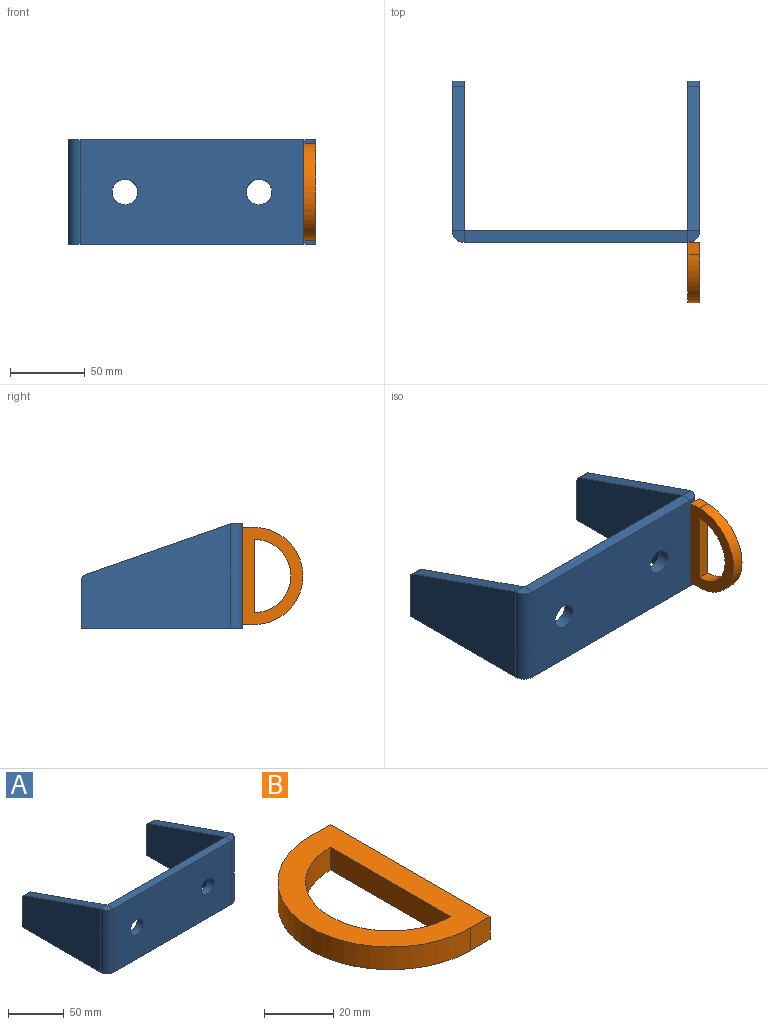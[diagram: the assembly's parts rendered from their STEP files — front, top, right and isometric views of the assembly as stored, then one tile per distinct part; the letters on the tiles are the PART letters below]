
ASSEMBLY  parts=2 mates=1
PART A: 26 faces, bbox 166x108x70 mm
  f0: plane 149.98x8mm, normal (0,0,-1), area 1199.8mm2, adj f4,f5,f13,f23
  f1: plane 149.99x8mm, normal (0,0,1), area 1199.8mm2, adj f4,f5,f12,f22
  f2: cylinder r=8.5mm len=17mm, axis (0,-1,0), area 427.3mm2, adj f4,f5
  f3: cylinder r=8.5mm len=17mm, axis (0,-1,0), area 427.3mm2, adj f4,f5
  f4: plane 149.98x70mm, normal (0,-1,0), area 10044.6mm2, adj f0,f1,f2,f3,f14,f24
  f5: plane 149.99x70mm, normal (0,1,0), area 10044.6mm2, adj f0,f1,f2,f3,f15,f25
  f6: plane 31.45x8mm, normal (0,1,0), area 251.6mm2, adj f7,f9,f10,f11
  f7: plane 99.99x8mm, normal (0,0,-1), area 799.9mm2, adj f6,f9,f10,f13
  f8: plane 96.65x33.83mm, normal (0,0.33,0.94), area 819.1mm2, adj f9,f10,f11,f12
  f9: plane 99.99x70mm, normal (-1,0,0), area 5247.2mm2, adj f6,f7,f8,f11,f14
  f10: plane 99.99x70mm, normal (1,0,0), area 5247.2mm2, adj f6,f7,f8,f11,f15
  f11: cylinder r=5mm len=8mm, axis (1,0,0), area 49.4mm2, adj f6,f8,f9,f10
  f12: plane 8.01x8.01mm, normal (0,0,1), area 50.4mm2, adj f1,f8,f14
  f13: plane 8.01x8.01mm, normal (0,0,-1), area 50.4mm2, adj f0,f7,f14,f15
  f14: cylinder r=8.01mm len=70mm, axis (0,0,1), area 880.8mm2, adj f4,f9,f12,f13
  f15: cylinder r=0.01mm len=70mm, axis (0,0,1), area 1.1mm2, adj f5,f10,f13
  f16: plane 99.99x8mm, normal (0,0,-1), area 799.9mm2, adj f17,f19,f20,f23
  f17: plane 31.45x8mm, normal (0,1,0), area 251.6mm2, adj f16,f19,f20,f21
  f18: plane 96.64x33.83mm, normal (0,0.33,0.94), area 819.1mm2, adj f19,f20,f21,f22
  f19: plane 99.99x70mm, normal (1,0,0), area 5247.2mm2, adj f16,f17,f18,f21,f24
  f20: plane 99.99x70mm, normal (-1,0,0), area 5247.2mm2, adj f16,f17,f18,f21,f25
  f21: cylinder r=5mm len=8mm, axis (-1,0,0), area 49.4mm2, adj f17,f18,f19,f20
  f22: plane 8.01x8.01mm, normal (0,0,1), area 50.4mm2, adj f1,f18,f24,f25
  f23: plane 8.01x8.01mm, normal (0,0,-1), area 50.4mm2, adj f0,f16,f24,f25
  f24: cylinder r=8.01mm len=70mm, axis (0,0,1), area 880.8mm2, adj f4,f19,f22,f23
  f25: cylinder r=0.01mm len=70mm, axis (0,0,1), area 1.1mm2, adj f5,f20,f22,f23
PART B: 8 faces, bbox 40.5x65x8 mm
  f0: plane 49x8mm, normal (-1,0,0), area 392mm2, adj f5,f6,f7
  f1: plane 65x8mm, normal (1,0,0), area 520mm2, adj f2,f4,f6,f7
  f2: plane 8x8mm, normal (0,-1,0), area 64mm2, adj f1,f3,f6,f7
  f3: cylinder r=32.5mm len=65mm, axis (0,0,-1), area 816.8mm2, adj f2,f4,f6,f7
  f4: plane 8x8mm, normal (0,1,0), area 64mm2, adj f1,f3,f6,f7
  f5: cylinder r=24.5mm len=49mm, axis (0,0,-1), area 615.8mm2, adj f0,f6,f7
  f6: plane 65x40.5mm, normal (0,0,-1), area 1236.3mm2, adj f0,f1,f2,f3,f4,f5
  f7: plane 65x40.5mm, normal (0,0,1), area 1236.3mm2, adj f0,f1,f2,f3,f4,f5
PLACE A t=(-24.32,-29.29,-16.76)mm
PLACE B rot(axis=(0.58,0.58,0.58),120deg) t=(133.67,-97.29,-21.76)mm
MATE fastened B.f1 <-> A.f4  axis (0,1,0) through (125.67,-37.29,18.24)mm
